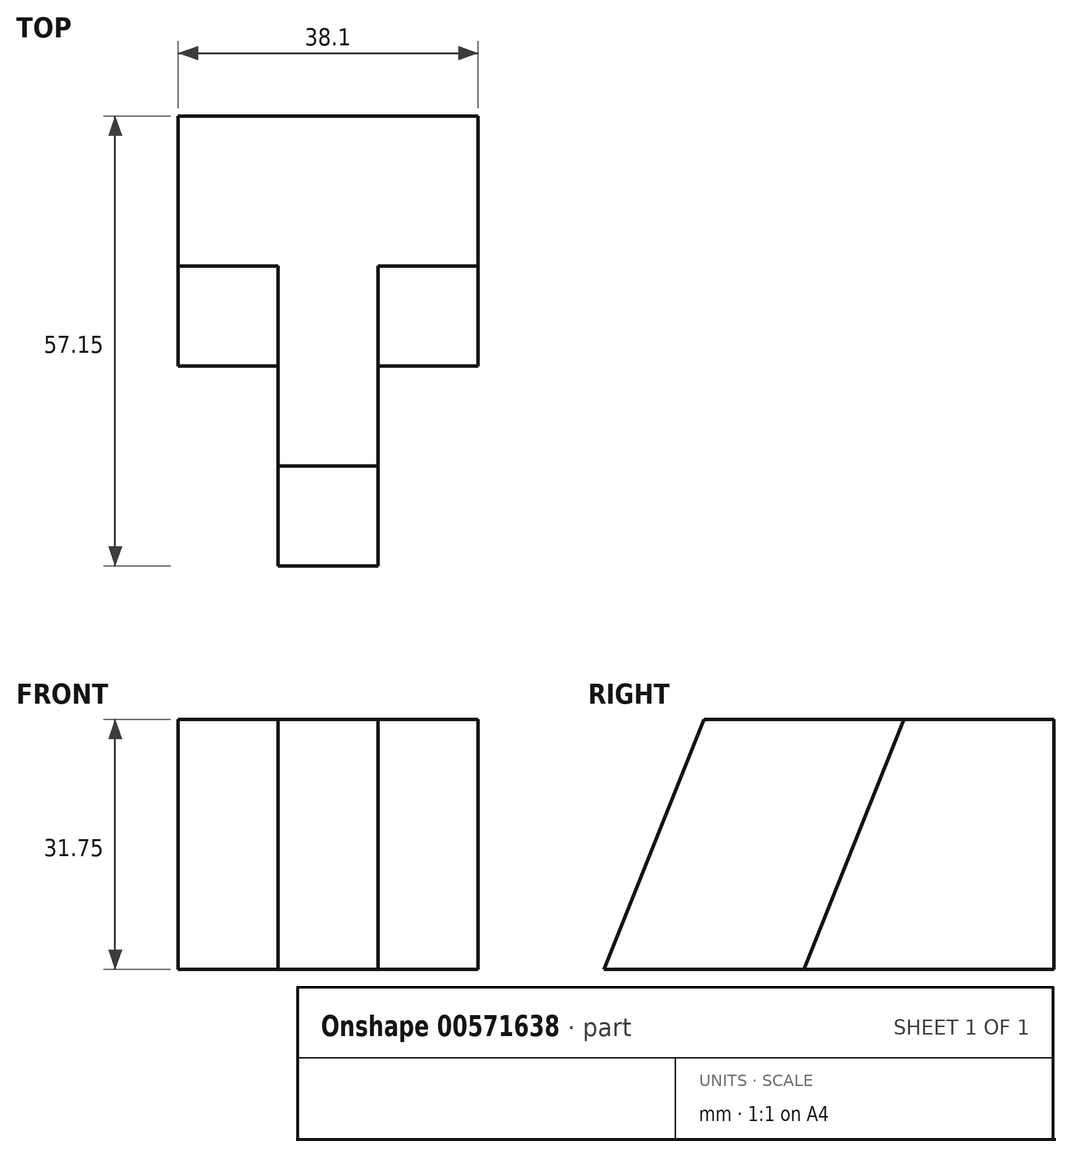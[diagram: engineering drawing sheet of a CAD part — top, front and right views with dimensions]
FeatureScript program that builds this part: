
annotation { "Feature Type Name" : "Feature", "Feature Type Description" : "" }
export const myFeature = defineFeature(function(context is Context, id is Id, definition is map)
    precondition{}
    {
        {
            var Q0;
            Q0=qCreatedBy(makeId("Top.planeOp"),FACE);
            var sketch = newSketch(context, id + "F0", { "sketchPlane" : qUnion([Q0])});
            skLineSegment(sketch, "E0", {"start": v(-45.75, 40.06) * mm, "end": v(-45.75, 21.01) * mm});
            skLineSegment(sketch, "E1", {"start": v(-45.75, 21.01) * mm, "end": v(-33.05, 21.01) * mm});
            skLineSegment(sketch, "E2", {"start": v(-33.05, 21.01) * mm, "end": v(-33.05, -4.39) * mm});
            skLineSegment(sketch, "E3", {"start": v(-33.05, -4.39) * mm, "end": v(-20.35, -4.39) * mm});
            skLineSegment(sketch, "E4", {"start": v(-20.35, -4.39) * mm, "end": v(-20.35, 21.01) * mm});
            skLineSegment(sketch, "E5", {"start": v(-20.35, 21.01) * mm, "end": v(-7.66, 21.01) * mm});
            skLineSegment(sketch, "E6", {"start": v(-7.66, 21.01) * mm, "end": v(-7.66, 40.06) * mm});
            skLineSegment(sketch, "E7", {"start": v(-7.66, 40.06) * mm, "end": v(-45.75, 40.06) * mm});
            skSolve(sketch);
        }
        {
            var Q0;
            Q0 = qSketchRegion(id + "F0", true);
            extrude(context, id + "F1", {"entities" : qUnion([Q0]), "depth" : 31.75 * mm, "offsetDistance" : 25.4 * mm});
        }
        {
            var Q0;
            Q0=makeQuery(id+"F1.opExtrude","SWEPT_FACE",FACE,{"disambiguationData":[OSD([sQuery(id+"F0.wireOp",EDGE,"E0")])]});
            var sketch = newSketch(context, id + "F2", { "sketchPlane" : qUnion([Q0])});
            skLineSegment(sketch, "E8", {"start": v(-21.01, 0) * mm, "end": v(-8.31, 0) * mm});
            skLineSegment(sketch, "E9", {"start": v(-8.31, 0) * mm, "end": v(-21.01, 31.75) * mm});
            skLineSegment(sketch, "E10", {"start": v(-21.01, 31.75) * mm, "end": v(-21.01, 0) * mm});
            skSolve(sketch);
        }
        {
            var Q0;
            Q0=makeQuery(id+"F2.imprint","IMPRINT",FACE,{"disambiguationData":[TD([[makeQuery(id+"F2.imprint","IMPRINT",EDGE,{"derivedFrom":sQuery(id+"F2.wireOp",EDGE,"E8")}),1.0]])]});
            extrude(context, id + "F3", {"entities" : qUnion([Q0]), "operationType" : NewBodyOperationType.ADD, "oppositeDirection" : true, "depth" : 38.1 * mm, "offsetDistance" : 25.4 * mm});
        }
        {
            var Q0;
            Q0=makeQuery(id+"F1.opExtrude","SWEPT_FACE",FACE,{"disambiguationData":[OSD([sQuery(id+"F0.wireOp",EDGE,"E2")])]});
            var sketch = newSketch(context, id + "F4", { "sketchPlane" : qUnion([Q0])});
            skLineSegment(sketch, "E11", {"start": v(4.39, 31.75) * mm, "end": v(4.39, 0) * mm});
            skLineSegment(sketch, "E12", {"start": v(4.39, 0) * mm, "end": v(17.09, 0) * mm});
            skLineSegment(sketch, "E13", {"start": v(17.09, 0) * mm, "end": v(4.39, 31.75) * mm});
            skSolve(sketch);
        }
        {
            var Q0;
            Q0=makeQuery(id+"F4.imprint","IMPRINT",FACE,{"disambiguationData":[TD([[makeQuery(id+"F4.imprint","IMPRINT",EDGE,{"derivedFrom":sQuery(id+"F4.wireOp",EDGE,"E11")}),1.0]])]});
            extrude(context, id + "F5", {"entities" : qUnion([Q0]), "operationType" : NewBodyOperationType.ADD, "oppositeDirection" : true, "depth" : 12.7 * mm, "offsetDistance" : 25.4 * mm});
        }
    });
